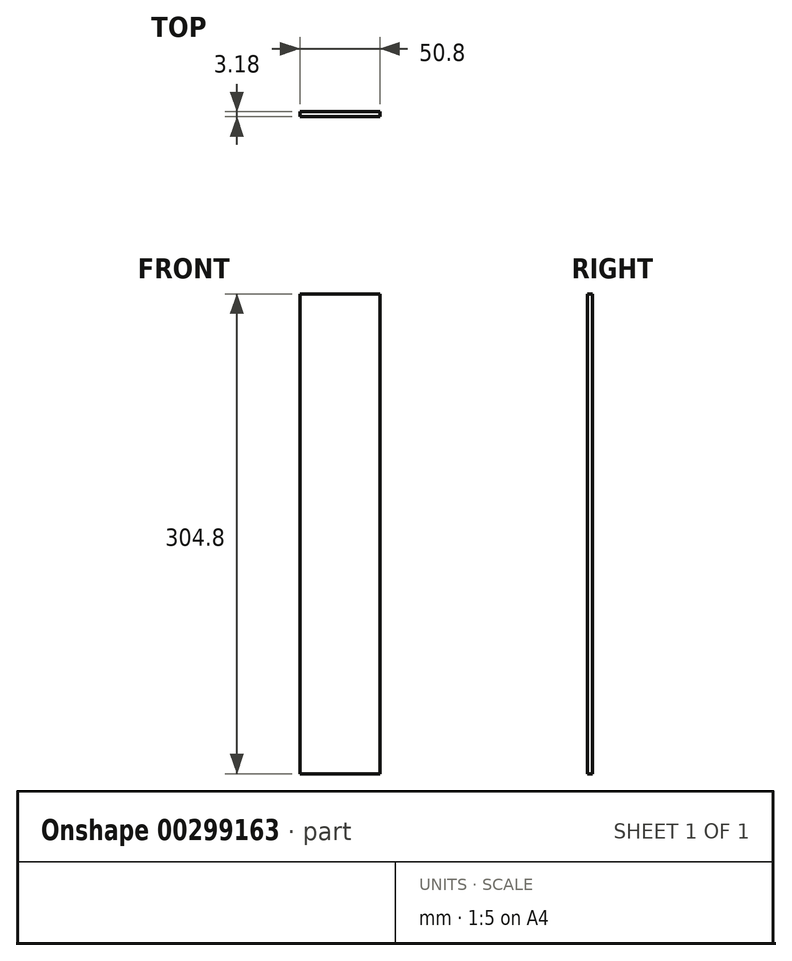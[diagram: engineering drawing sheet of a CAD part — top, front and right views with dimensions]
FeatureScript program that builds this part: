
annotation { "Feature Type Name" : "Feature", "Feature Type Description" : "" }
export const myFeature = defineFeature(function(context is Context, id is Id, definition is map)
    precondition{}
    {
        {
            var Q0;
            Q0=qCreatedBy(makeId("Front.planeOp"),FACE);
            var sketch = newSketch(context, id + "F0", { "sketchPlane" : qUnion([Q0])});
            skLineSegment(sketch, "E0.bottom", {"start": v(-25.4, 152.4) * mm, "end": v(25.4, 152.4) * mm});
            skLineSegment(sketch, "E0.top", {"start": v(-25.4, -152.4) * mm, "end": v(25.4, -152.4) * mm});
            skLineSegment(sketch, "E0.left", {"start": v(-25.4, 152.4) * mm, "end": v(-25.4, -152.4) * mm});
            skLineSegment(sketch, "E0.right", {"start": v(25.4, 152.4) * mm, "end": v(25.4, -152.4) * mm});
            skPoint(sketch, "E0.middle", {"position": v(0, 0) * mm});
            skSolve(sketch);
        }
        {
            var Q0;
            Q0 = qSketchRegion(id + "F0", true);
            extrude(context, id + "F1", {"entities" : qUnion([Q0]), "endBound" : BoundingType.SYMMETRIC, "depth" : 3.17 * mm});
        }
    });
